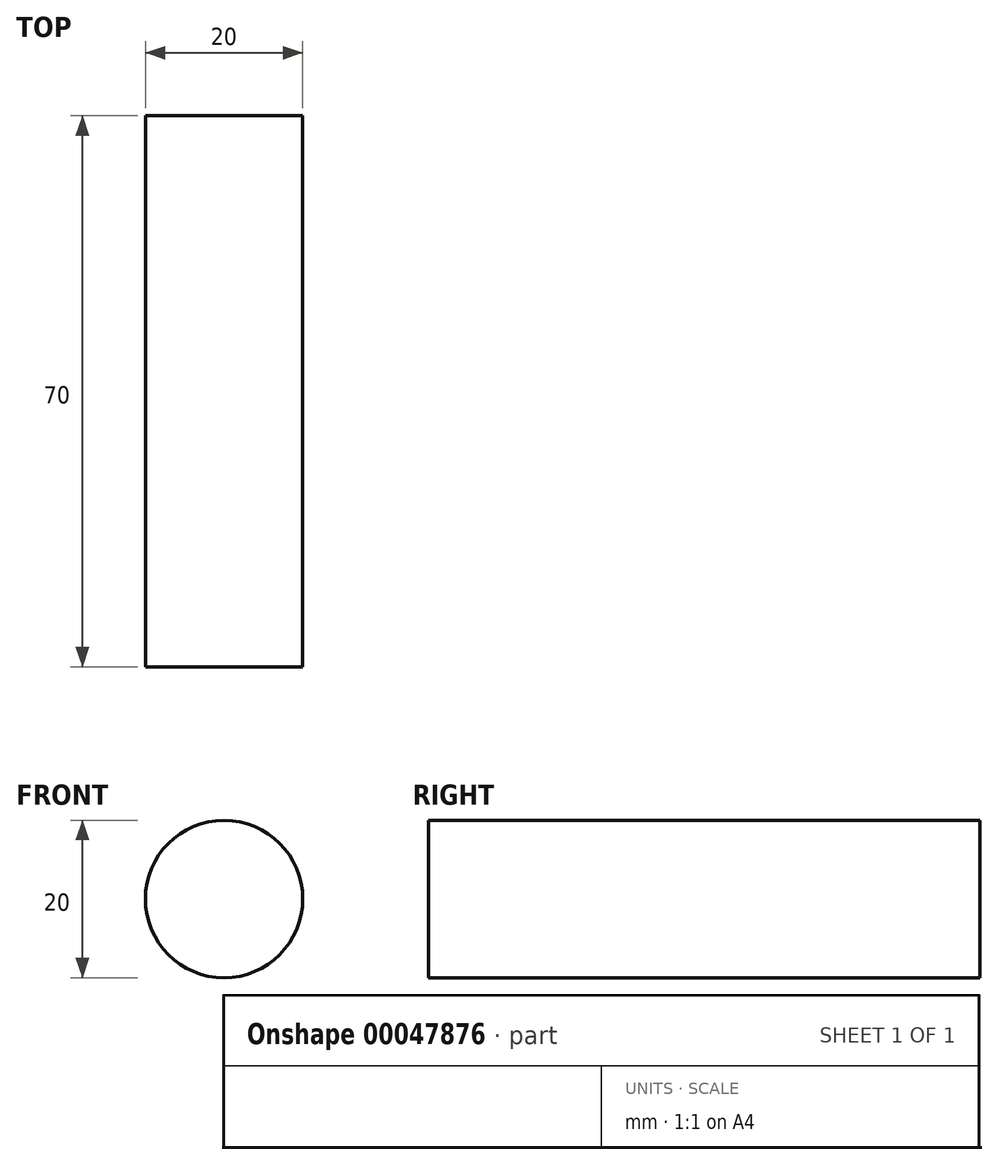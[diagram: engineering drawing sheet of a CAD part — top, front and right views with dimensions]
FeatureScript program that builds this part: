
annotation { "Feature Type Name" : "Feature", "Feature Type Description" : "" }
export const myFeature = defineFeature(function(context is Context, id is Id, definition is map)
    precondition{}
    {
        {
            var Q0;
            Q0=qCreatedBy(makeId("Front.planeOp"),FACE);
            var sketch = newSketch(context, id + "F0", { "sketchPlane" : qUnion([Q0])});
            skCircle(sketch, "E0", {"center": v(0, 0) * mm, "radius": 10 * mm});
            skSolve(sketch);
        }
        {
            var Q0;
            Q0=makeQuery(id+"F0.imprint","IMPRINT",FACE,{"disambiguationData":[TD([[makeQuery(id+"F0.imprint","IMPRINT",EDGE,{"derivedFrom":sQuery(id+"F0.wireOp",EDGE,"E0")}),1.0]])]});
            extrude(context, id + "F1", {"entities" : qUnion([Q0]), "depth" : 70 * mm});
        }
    });
